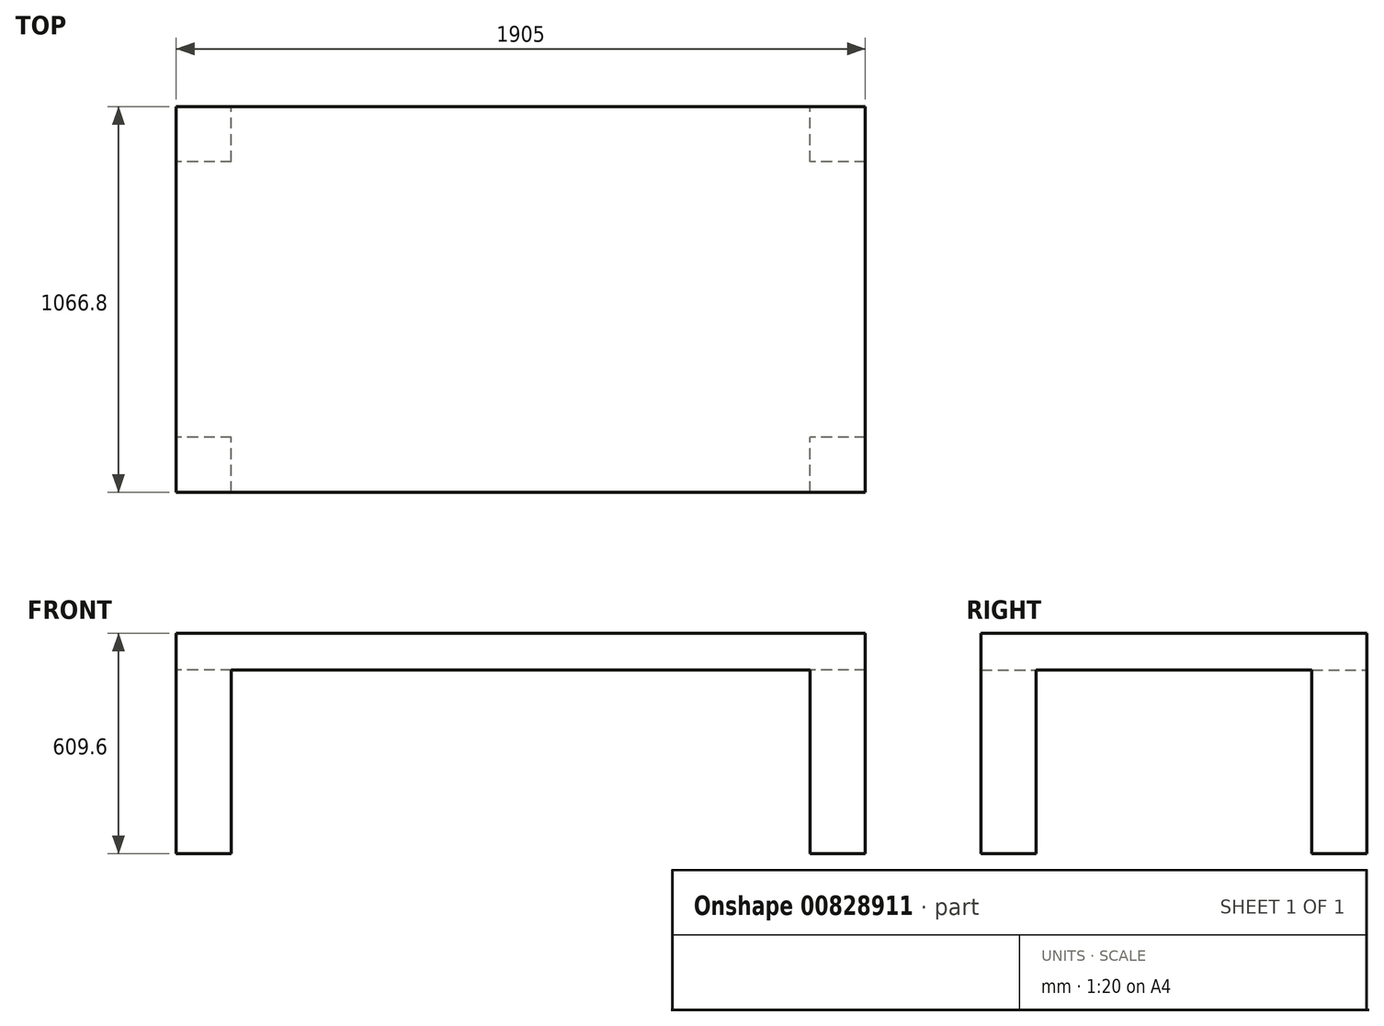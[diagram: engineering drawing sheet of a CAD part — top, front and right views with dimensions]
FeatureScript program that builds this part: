
annotation { "Feature Type Name" : "Feature", "Feature Type Description" : "" }
export const myFeature = defineFeature(function(context is Context, id is Id, definition is map)
    precondition{}
    {
        {
            var Q0;
            Q0=qCreatedBy(makeId("Top.planeOp"),FACE);
            var sketch = newSketch(context, id + "F0", { "sketchPlane" : qUnion([Q0])});
            skLineSegment(sketch, "E0.bottom", {"start": v(952.5, -533.4) * mm, "end": v(-952.5, -533.4) * mm});
            skLineSegment(sketch, "E0.top", {"start": v(952.5, 533.4) * mm, "end": v(-952.5, 533.4) * mm});
            skLineSegment(sketch, "E0.left", {"start": v(952.5, -533.4) * mm, "end": v(952.5, 533.4) * mm});
            skLineSegment(sketch, "E0.right", {"start": v(-952.5, -533.4) * mm, "end": v(-952.5, 533.4) * mm});
            skPoint(sketch, "E0.middle", {"position": v(0, 0) * mm});
            skSolve(sketch);
        }
        {
            var Q0;
            Q0 = qSketchRegion(id + "F0", true);
            extrude(context, id + "F1", {"entities" : qUnion([Q0]), "depth" : 609.6 * mm, "offsetDistance" : 25.4 * mm});
        }
        {
            var Q0;
            Q0=makeQuery(id+"F1.opExtrude","CAP_FACE",FACE,{"disambiguationData":[OSD([sQuery(id+"F0.wireOp",EDGE,"E0.bottom"),sQuery(id+"F0.wireOp",EDGE,"E0.top"),sQuery(id+"F0.wireOp",EDGE,"E0.left"),sQuery(id+"F0.wireOp",EDGE,"E0.right")])],"isStart":true});
            var sketch = newSketch(context, id + "F2", { "sketchPlane" : qUnion([Q0])});
            skLineSegment(sketch, "E1.bottom", {"start": v(952.5, 381) * mm, "end": v(800.1, 381) * mm});
            skLineSegment(sketch, "E1.top", {"start": v(952.5, -381) * mm, "end": v(800.1, -381) * mm});
            skLineSegment(sketch, "E1.left", {"start": v(952.5, 381) * mm, "end": v(952.5, -381) * mm});
            skLineSegment(sketch, "E1.right", {"start": v(-952.5, 381) * mm, "end": v(-952.5, -381) * mm});
            skPoint(sketch, "E1.middle", {"position": v(0, 0) * mm});
            skLineSegment(sketch, "E2.bottom", {"start": v(800.1, 533.4) * mm, "end": v(-800.1, 533.4) * mm});
            skLineSegment(sketch, "E2.top", {"start": v(800.1, -533.4) * mm, "end": v(-800.1, -533.4) * mm});
            skLineSegment(sketch, "E2.left", {"start": v(800.1, 533.4) * mm, "end": v(800.1, 381) * mm});
            skLineSegment(sketch, "E2.right", {"start": v(-800.1, 533.4) * mm, "end": v(-800.1, 381) * mm});
            skLineSegment(sketch, "E3.trimOffspring", {"start": v(-800.1, 381) * mm, "end": v(-952.5, 381) * mm});
            skLineSegment(sketch, "E4.trimOffspring", {"start": v(-800.1, -381) * mm, "end": v(-800.1, -533.4) * mm});
            skLineSegment(sketch, "E5.trimOffspring", {"start": v(-800.1, -381) * mm, "end": v(-952.5, -381) * mm});
            skLineSegment(sketch, "E6.trimOffspring", {"start": v(800.1, -381) * mm, "end": v(800.1, -533.4) * mm});
            skSolve(sketch);
        }
        {
            var Q0;
            Q0 = qSketchRegion(id + "F2", true);
            extrude(context, id + "F3", {"entities" : qUnion([Q0]), "operationType" : NewBodyOperationType.REMOVE, "oppositeDirection" : true, "depth" : 508 * mm, "offsetDistance" : 25.4 * mm});
        }
    });
